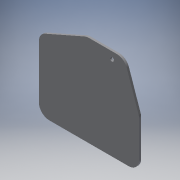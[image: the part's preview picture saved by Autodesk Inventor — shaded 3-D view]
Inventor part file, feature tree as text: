
AUTODESK INVENTOR PART (.ipt)
format: ipt  version: 2016 (Build 200138000, 138)  size: 107,008 bytes
history: native  units: mm
features: extrude x1, fillet x1, reference x1
ambient origin geometry x8: Origin, YZ Plane, XZ Plane, XY Plane, X Axis, Y Axis, Z Axis, Center Point
bodies: Body1 (feature_tree)
feature tree (3):
  extrude  "Extrusion2"  Depth=145.0mm
  fillet  "Fillet1"  Radius=3.0mm
  reference  "Reference1"
